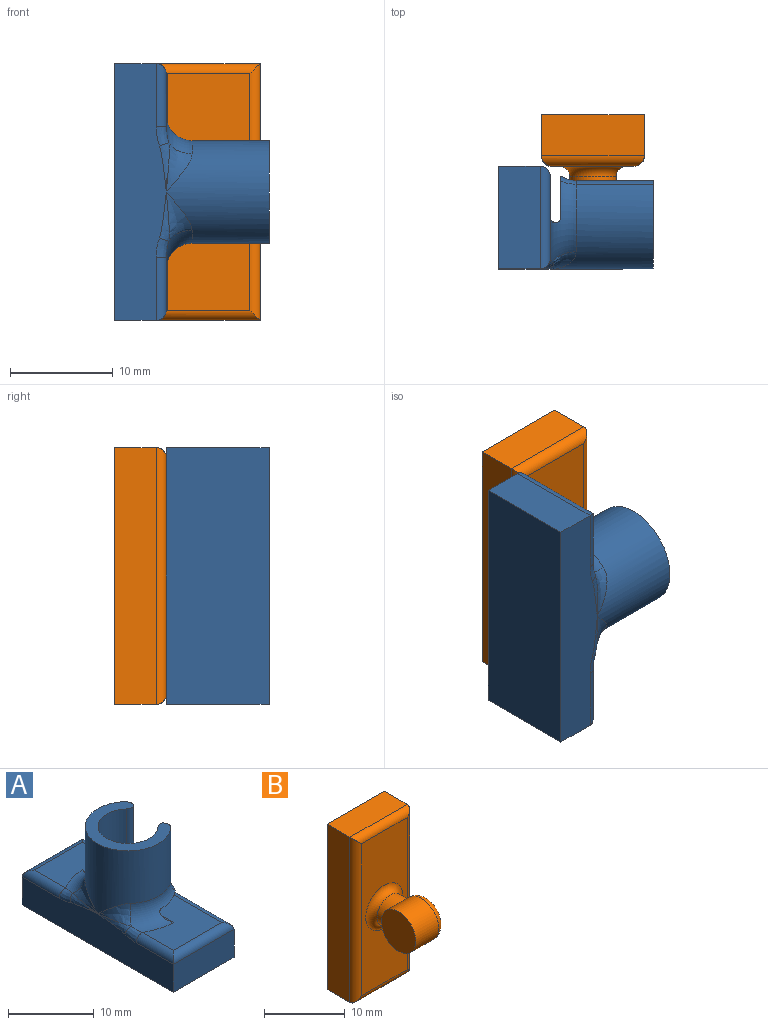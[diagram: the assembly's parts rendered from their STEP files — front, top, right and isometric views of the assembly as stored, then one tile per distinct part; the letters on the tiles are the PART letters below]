
ASSEMBLY  parts=2 mates=1
PART A: 32 faces, bbox 13.2x25x15 mm
  f0: plane 25x4mm, normal (1,0,0), area 100mm2, adj f1,f3,f5,f27
  f1: plane 10x4mm, normal (0,1,0), area 40mm2, adj f0,f2,f5,f26
  f2: plane 25x5mm, normal (-1,0,0), area 106.9mm2, adj f1,f3,f5,f23,f24,f25,f29,f30
  f3: plane 10x4mm, normal (0,-1,0), area 40mm2, adj f0,f2,f5,f28
  f4: plane 23x8mm, normal (0,0,1), area 146.2mm2, adj f6,f10,f11,f18,f21,f25,f26,f27
  f5: plane 25x10mm, normal (0,0,-1), area 250mm2, adj f0,f1,f2,f3
  f6: cylinder r=3.5mm len=10mm, axis (0,0,-1), area 155.5mm2, adj f4,f8,f9,f10,f11,f12,f14,f16
  f7: cylinder r=5mm len=10mm, axis (0,0,-1), area 181.4mm2, adj f8,f13,f15,f17,f18,f21,f22
  f8: plane 10x8.6mm, normal (0,0,1), area 31.4mm2, adj f6,f7,f13,f14,f15,f16
  f9: plane 4.02x3.16mm, normal (0,0,-1), area 8.2mm2, adj f6,f10,f16,f20,f21
  f10: cylinder r=0.5mm len=4mm, axis (0,-1,0), area 4.7mm2, adj f4,f6,f9,f21
  f11: cylinder r=0.5mm len=4mm, axis (0,-1,0), area 4.7mm2, adj f4,f6,f12,f18
  f12: plane 4.02x3.16mm, normal (0,0,-1), area 8.2mm2, adj f6,f11,f14,f18,f19
  f13: cylinder r=1mm len=7.5mm, axis (0,0,-1), area 11.7mm2, adj f7,f8,f14,f19
  f14: cylinder r=1mm len=9mm, axis (0,0,-1), area 10.9mm2, adj f6,f8,f12,f13,f19
  f15: cylinder r=1mm len=7.5mm, axis (0,0,-1), area 11.7mm2, adj f7,f8,f16,f20
  f16: cylinder r=1mm len=9mm, axis (0,0,-1), area 10.9mm2, adj f6,f8,f9,f15,f20
  f17: bspline ~5.59x2.5mm, area 6.9mm2, adj f7,f18,f23
  f18: torus R=7.5mm, axis (0,0,1), area 21.4mm2, adj f4,f7,f11,f12,f17,f19,f24
  f19: torus R=3.5mm, axis (0,0,1), area 1.8mm2, adj f12,f13,f14,f18
  f20: torus R=3.5mm, axis (0,0,1), area 1.8mm2, adj f9,f15,f16,f21
  f21: torus R=7.5mm, axis (0,0,1), area 21.4mm2, adj f4,f7,f9,f10,f20,f22,f30
  f22: bspline ~5.8x2.66mm, area 6.9mm2, adj f7,f21,f31
  f23: bspline ~4.8x0.95mm, area 2.5mm2, adj f2,f17,f24
  f24: bspline ~3.67x1.49mm, area 2.4mm2, adj f2,f18,f23,f25
  f25: cylinder r=1mm len=6.16mm, axis (0,1,0), area 8.9mm2, adj f2,f4,f24,f26
  f26: cylinder r=1mm len=10mm, axis (1,0,0), area 14.1mm2, adj f1,f4,f25,f27
  f27: cylinder r=1mm len=25mm, axis (0,-1,0), area 37.7mm2, adj f0,f4,f26,f28
  f28: cylinder r=1mm len=10mm, axis (-1,0,0), area 14.1mm2, adj f3,f4,f27,f29
  f29: cylinder r=1mm len=6.16mm, axis (0,1,0), area 8.9mm2, adj f2,f4,f28,f30
  f30: bspline ~3.67x1.49mm, area 2.4mm2, adj f2,f21,f29,f31
  f31: bspline ~4.8x0.95mm, area 1.7mm2, adj f2,f22,f30
PART B: 17 faces, bbox 10x13.2x25 mm
  f0: cylinder r=2.25mm len=4.5mm, axis (0,1,0), area 20.9mm2, adj f7,f11,f12
  f1: plane 10x4mm, normal (0,0,-1), area 40mm2, adj f2,f4,f6,f13
  f2: plane 25x4mm, normal (1,0,0), area 100mm2, adj f1,f3,f6,f14
  f3: plane 10x4mm, normal (0,0,1), area 40mm2, adj f2,f4,f6,f16
  f4: plane 25x4mm, normal (-1,0,0), area 100mm2, adj f1,f3,f6,f15
  f5: plane 23x8mm, normal (0,-1,0), area 150.8mm2, adj f12,f13,f14,f15,f16
  f6: plane 25x10mm, normal (0,1,0), area 250mm2, adj f1,f2,f3,f4
  f7: cylinder r=3mm len=6mm, axis (1,0,0), area 59.8mm2, adj f0,f8,f10
  f8: plane 6x6mm, normal (-1,0,0), area 28.3mm2, adj f7
  f9: plane 4.34x4mm, normal (1,0,0), area 12.9mm2, adj f10,f11
  f10: torus R=2mm, axis (-1,0,0), area 21.1mm2, adj f7,f9,f11
  f11: bspline ~3.56x1.42mm, area 3.3mm2, adj f0,f9,f10
  f12: torus R=3.25mm, axis (0,-1,0), area 25.8mm2, adj f0,f5
  f13: cylinder r=1mm len=10mm, axis (-1,0,0), area 14.6mm2, adj f1,f5,f14,f15
  f14: cylinder r=1mm len=25mm, axis (0,0,-1), area 38.1mm2, adj f2,f5,f13,f16
  f15: cylinder r=1mm len=25mm, axis (0,0,1), area 38.1mm2, adj f4,f5,f13,f16
  f16: cylinder r=1mm len=10mm, axis (1,0,0), area 14.6mm2, adj f3,f5,f14,f15
PLACE A rot(axis=(0.58,0.58,0.58),120deg) t=(-22.65,-22.26,-0.95)mm
PLACE B t=(-13.5,-12.26,-0.95)mm fixed
MATE slider A.f6 <-> B.f7  axis (-1,0,0) through (-12.65,-22.26,-0.95)mm
